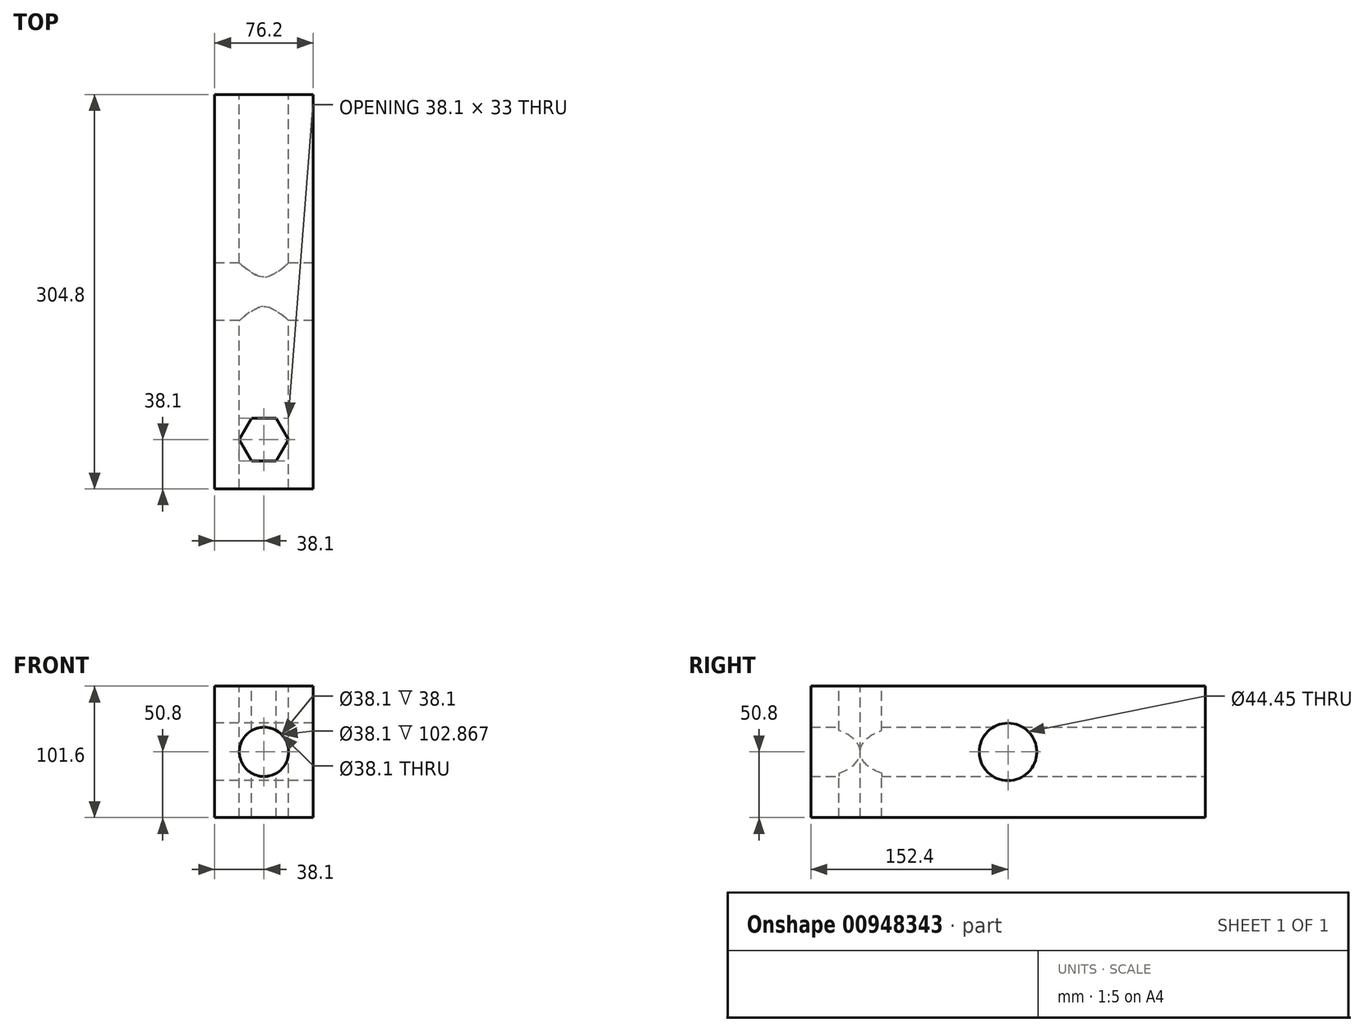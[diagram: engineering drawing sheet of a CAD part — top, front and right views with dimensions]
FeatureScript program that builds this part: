
annotation { "Feature Type Name" : "Feature", "Feature Type Description" : "" }
export const myFeature = defineFeature(function(context is Context, id is Id, definition is map)
    precondition{}
    {
        {
            var Q0;
            Q0=qCreatedBy(makeId("Front.planeOp"),FACE);
            var sketch = newSketch(context, id + "F0", { "sketchPlane" : qUnion([Q0])});
            skLineSegment(sketch, "E0.bottom", {"start": v(38.1, 50.8) * mm, "end": v(-38.1, 50.8) * mm});
            skLineSegment(sketch, "E0.top", {"start": v(38.1, -50.8) * mm, "end": v(-38.1, -50.8) * mm});
            skLineSegment(sketch, "E0.left", {"start": v(38.1, 50.8) * mm, "end": v(38.1, -50.8) * mm});
            skLineSegment(sketch, "E0.right", {"start": v(-38.1, 50.8) * mm, "end": v(-38.1, -50.8) * mm});
            skPoint(sketch, "E0.middle", {"position": v(0, 0) * mm});
            skCircle(sketch, "E1", {"center": v(0, 0) * mm, "radius": 19.05 * mm});
            skSolve(sketch);
        }
        {
            var Q0;
            Q0 = qSketchRegion(id + "F0", true);
            extrude(context, id + "F1", {"entities" : qUnion([Q0]), "endBound" : BoundingType.SYMMETRIC, "depth" : 304.8 * mm, "offsetDistance" : 25.4 * mm});
        }
        {
            var Q0;
            Q0=qCreatedBy(makeId("Right.planeOp"),FACE);
            var sketch = newSketch(context, id + "F2", { "sketchPlane" : qUnion([Q0])});
            skCircle(sketch, "E2", {"center": v(0, 0) * mm, "radius": 22.23 * mm});
            skSolve(sketch);
        }
        {
            var Q0;
            Q0 = qSketchRegion(id + "F2", true);
            extrude(context, id + "F3", {"entities" : qUnion([Q0]), "operationType" : NewBodyOperationType.REMOVE, "endBound" : BoundingType.THROUGH_ALL, "depth" : 239.1 * mm, "offsetDistance" : 25.4 * mm, "hasSecondDirection" : true, "secondDirectionOppositeDirection" : true, "secondDirectionDepth" : 139.23 * mm});
        }
        {
            var Q0;
            Q0=makeQuery(id+"F1.opExtrude","SWEPT_FACE",FACE,{"disambiguationData":[OSD([sQuery(id+"F0.wireOp",EDGE,"E0.bottom")])]});
            var sketch = newSketch(context, id + "F4", { "sketchPlane" : qUnion([Q0])});
            skCircle(sketch, "E3.cCircle", {"center": v(0, -114.3) * mm, "radius": 19.05 * mm, "construction": true});
            skLineSegment(sketch, "E3.0", {"start": v(-9.52, -97.8) * mm, "end": v(9.53, -97.8) * mm});
            skLineSegment(sketch, "E3.1", {"start": v(9.52, -97.8) * mm, "end": v(19.05, -114.3) * mm});
            skLineSegment(sketch, "E3.2", {"start": v(19.05, -114.3) * mm, "end": v(9.53, -130.8) * mm});
            skLineSegment(sketch, "E3.3", {"start": v(9.53, -130.8) * mm, "end": v(-9.52, -130.8) * mm});
            skLineSegment(sketch, "E3.4", {"start": v(-9.52, -130.8) * mm, "end": v(-19.05, -114.3) * mm});
            skLineSegment(sketch, "E3.5", {"start": v(-19.05, -114.3) * mm, "end": v(-9.52, -97.8) * mm});
            skSolve(sketch);
        }
        {
            var Q0;
            Q0=makeQuery(id+"F4.imprint","IMPRINT",FACE,{"disambiguationData":[TD([[makeQuery(id+"F4.imprint","IMPRINT",EDGE,{"derivedFrom":sQuery(id+"F4.wireOp",EDGE,"E3.0")}),-1.0]])]});
            extrude(context, id + "F5", {"entities" : qUnion([Q0]), "operationType" : NewBodyOperationType.REMOVE, "endBound" : BoundingType.THROUGH_ALL, "oppositeDirection" : true, "depth" : 93.16 * mm, "offsetDistance" : 25.4 * mm});
        }
    });
